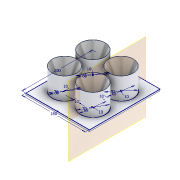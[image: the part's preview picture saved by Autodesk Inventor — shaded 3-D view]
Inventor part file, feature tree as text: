
AUTODESK INVENTOR PART (.ipt)
format: ipt  version: 2020.3 (Build 243373010, 373A)  size: 166,400 bytes
history: native  units: mm
features: sketch x2, plane x1, revolve x1, pattern_linear x1, extrude x1
ambient origin geometry x8: Origin, YZ Plane, XZ Plane, XY Plane, X Axis, Y Axis, Z Axis, Center Point
bodies: Solid1 (feature_tree)
feature tree (6):
  sketch  "Sketch1"  dims[d0=180.0mm d1=200.0mm]
  plane  "Work Plane1"
  revolve  "Revolution1"  [1 undecoded]
  pattern_linear  "Rectangular Pattern1"  Spacing1=10.0mm  [1 undecoded]
  extrude  "Extrusion1"  Depth=10.0mm
  sketch  "Sketch2"  dims[d2=70.0mm d3=70.0mm d4=70.0mm d5=70.0mm d6=10.0mm d7=10.0mm d8=68.0mm d9=68.0mm d10=68.0mm d11=68.0mm d12=10.0mm d13=10.0mm d14=10.0mm d15=10.0mm d16=-50.0mm d17=60.0mm d18=0.0mm d20=90.0deg d21=20.0mm d23=-80.0mm d24=20.0mm d26=80.0mm d27=5.0mm d28=0.0mm]
note: 2 required parameter values undecoded (feature->parameter linkage not recoverable at this tier; creation-order binding heuristic only, values carry confidence <= 0.55)